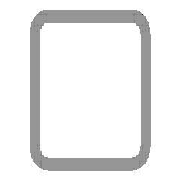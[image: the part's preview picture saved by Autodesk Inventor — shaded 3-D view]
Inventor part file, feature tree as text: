
AUTODESK INVENTOR PART (.ipt)
format: ipt  version: 2022.1 (Build 261234000, 234)  size: 171,008 bytes
history: native  units: mm (DEFAULTED — no unit token found)
features: plane x5, other x4, sketch x4, extrude x1, boolean_combine x1, split x1
ambient origin geometry x8: Origin, YZ Plane, XZ Plane, XY Plane, X Axis, Y Axis, Z Axis, Center Point
bodies: Solid1 (feature_tree), Body (feature_tree), Solid2 (feature_tree)
feature tree (16):
  parser-record x1  (decoder bookkeeping rows leaked as tree rows — omitted from the tree; the rows remain in map.json)
  other  "Driven Length"
  other  "Start Plane"
  other  "End Plane"
  plane  "Work Plane4"
  plane  "Work Plane5"
  plane  "Work Plane6"
  extrude  "Extrusion2"  TaperAngle=0.0deg  [1 undecoded]
  boolean_combine  "Combine1"
  plane  "Plano de trabajo7"
  split  "Dividir1"
  sketch  "Sketch"  dims[d11=40.0mm d12=2.0mm d13=20.0mm d14=480.0mm d15=20.0mm d16=20.0mm d17=90.0deg d18=460.0mm d19=0.12mm d20=0.0mm]
  sketch  "Sketch3"  dims[d3=444.0mm d4=0.0mm]
  plane  "Work Plane3"
  sketch  "Sketch4"  dims[d7=4.0mm]
  sketch  "Sketch5"  dims[d9=40.0mm]
note: 1 required parameter value undecoded (feature->parameter linkage not recoverable at this tier; creation-order binding heuristic only, values carry confidence <= 0.55)
